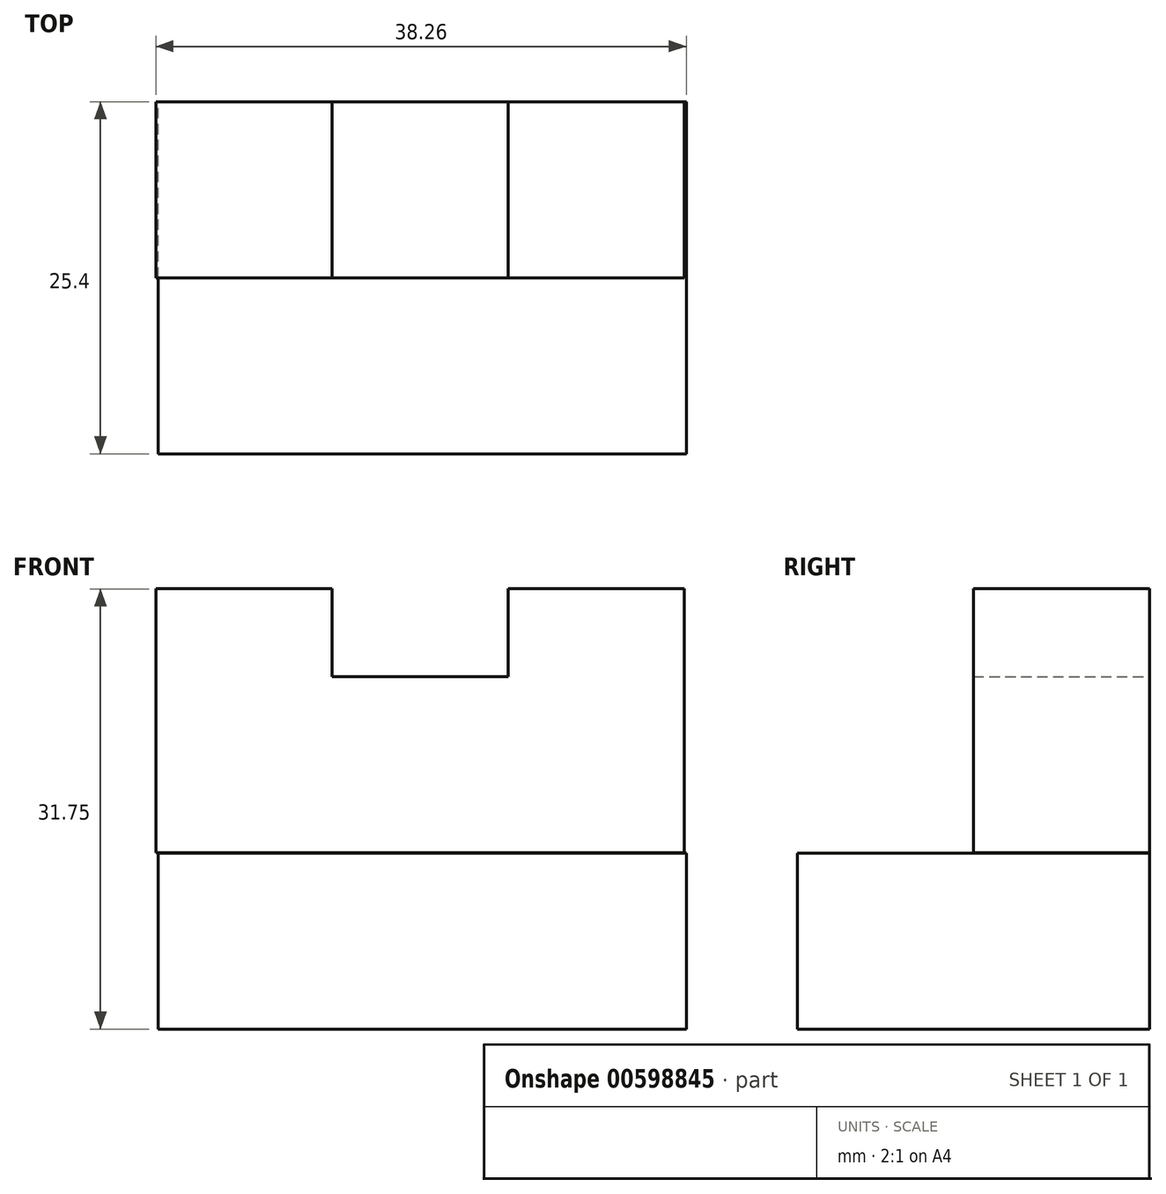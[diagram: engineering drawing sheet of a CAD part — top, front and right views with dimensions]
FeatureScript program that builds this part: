
annotation { "Feature Type Name" : "Feature", "Feature Type Description" : "" }
export const myFeature = defineFeature(function(context is Context, id is Id, definition is map)
    precondition{}
    {
        {
            var Q0;
            Q0=qCreatedBy(makeId("Front.planeOp"),FACE);
            var sketch = newSketch(context, id + "F0", { "sketchPlane" : qUnion([Q0])});
            skLineSegment(sketch, "E0", {"start": v(0, 0) * mm, "end": v(-19.05, 0) * mm});
            skLineSegment(sketch, "E1", {"start": v(0, 0) * mm, "end": v(19.05, 0) * mm});
            skLineSegment(sketch, "E2", {"start": v(19.05, 0) * mm, "end": v(19.05, 12.7) * mm});
            skLineSegment(sketch, "E3", {"start": v(-19.05, 0) * mm, "end": v(-19.05, 12.7) * mm});
            skLineSegment(sketch, "E4", {"start": v(-19.05, 12.7) * mm, "end": v(19.05, 12.7) * mm});
            skSolve(sketch);
        }
        {
            var Q0;
            Q0=makeQuery(id+"F0.imprint","IMPRINT",FACE,{"disambiguationData":[TD([[makeQuery(id+"F0.imprint","IMPRINT",EDGE,{"derivedFrom":sQuery(id+"F0.wireOp",EDGE,"E0")}),-1.0]])]});
            extrude(context, id + "F1", {"entities" : qUnion([Q0]), "depth" : 25.4 * mm, "offsetDistance" : 25.4 * mm});
        }
        {
            var Q0;
            Q0=qCreatedBy(makeId("Front.planeOp"),FACE);
            var sketch = newSketch(context, id + "F2", { "sketchPlane" : qUnion([Q0])});
            skLineSegment(sketch, "E5", {"start": v(-19.2, 12.7) * mm, "end": v(-19.2, 31.75) * mm});
            skLineSegment(sketch, "E6", {"start": v(-19.2, 31.75) * mm, "end": v(-6.5, 31.75) * mm});
            skLineSegment(sketch, "E7", {"start": v(-6.5, 31.75) * mm, "end": v(-6.5, 25.4) * mm});
            skLineSegment(sketch, "E8", {"start": v(-6.5, 25.4) * mm, "end": v(6.2, 25.4) * mm});
            skLineSegment(sketch, "E9", {"start": v(-19.2, 12.7) * mm, "end": v(18.9, 12.7) * mm});
            skLineSegment(sketch, "E10", {"start": v(18.9, 12.7) * mm, "end": v(18.9, 31.75) * mm});
            skLineSegment(sketch, "E11", {"start": v(18.9, 31.75) * mm, "end": v(6.2, 31.75) * mm});
            skLineSegment(sketch, "E12", {"start": v(6.2, 31.75) * mm, "end": v(6.2, 25.4) * mm});
            skSolve(sketch);
        }
        {
            var Q0;
            Q0=makeQuery(id+"F2.imprint","IMPRINT",FACE,{"disambiguationData":[TD([[makeQuery(id+"F2.imprint","IMPRINT",EDGE,{"derivedFrom":sQuery(id+"F2.wireOp",EDGE,"E5")}),-1.0]])]});
            extrude(context, id + "F3", {"entities" : qUnion([Q0]), "depth" : 12.7 * mm, "offsetDistance" : 25.4 * mm});
        }
    });
